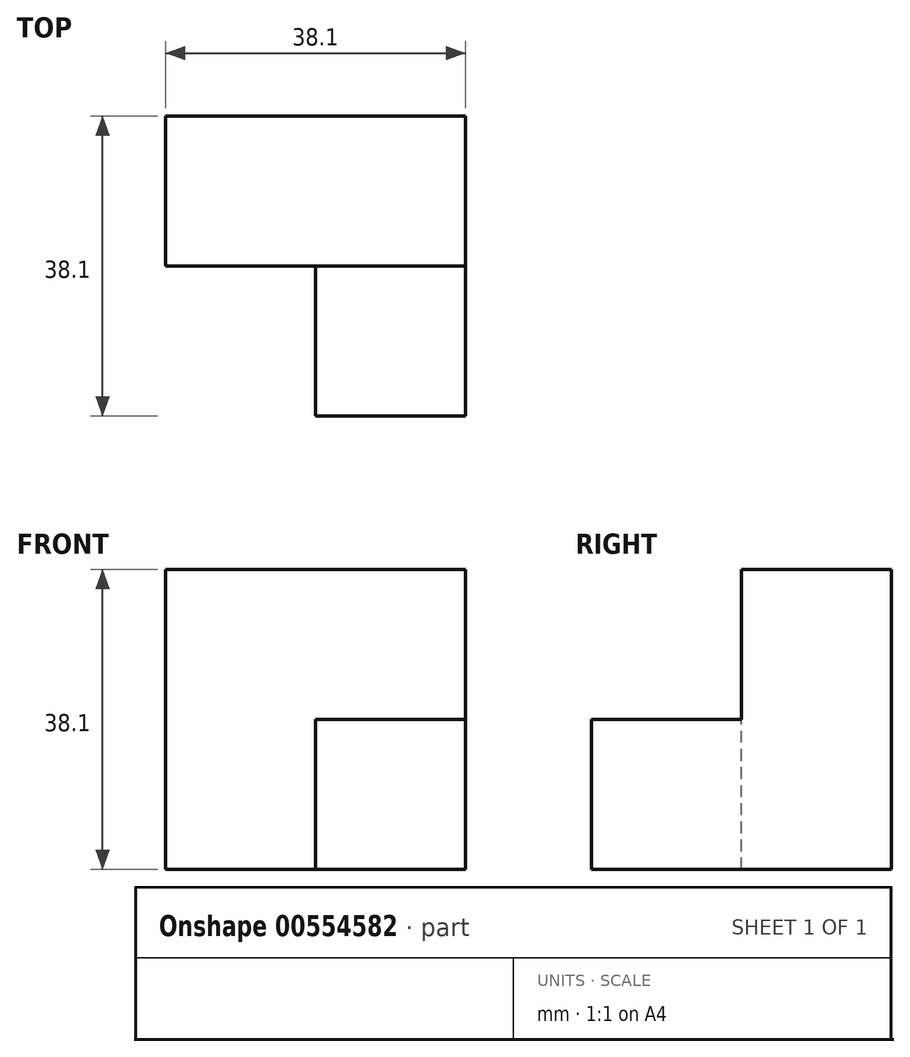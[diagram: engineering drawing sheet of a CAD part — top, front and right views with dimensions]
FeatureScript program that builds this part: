
annotation { "Feature Type Name" : "Feature", "Feature Type Description" : "" }
export const myFeature = defineFeature(function(context is Context, id is Id, definition is map)
    precondition{}
    {
        {
            var Q0;
            Q0=qCreatedBy(makeId("Front.planeOp"),FACE);
            var sketch = newSketch(context, id + "F0", { "sketchPlane" : qUnion([Q0])});
            skLineSegment(sketch, "E0", {"start": v(-17.43, 17.6) * mm, "end": v(20.67, 17.6) * mm});
            skLineSegment(sketch, "E1", {"start": v(20.67, 17.6) * mm, "end": v(20.67, -20.5) * mm});
            skLineSegment(sketch, "E2", {"start": v(20.67, -20.5) * mm, "end": v(-17.43, -20.5) * mm});
            skLineSegment(sketch, "E3", {"start": v(-17.43, -20.5) * mm, "end": v(-17.43, 17.6) * mm});
            skLineSegment(sketch, "E4", {"start": v(1.62, -20.5) * mm, "end": v(1.62, -1.46) * mm});
            skLineSegment(sketch, "E5", {"start": v(1.62, -1.46) * mm, "end": v(20.67, -1.46) * mm});
            skSolve(sketch);
        }
        {
            var Q0;
            {var subQ4=sQuery(id+"F0.wireOp",EDGE,"E0");Q0=makeQuery(id+"F0.imprint","IMPRINT",FACE,{"disambiguationData":[TD([[makeQuery(id+"F0.imprint","IMPRINT",EDGE,{"derivedFrom":subQ4}),-1.0]])]});}
            extrude(context, id + "F1", {"entities" : qUnion([Q0]), "depth" : 19.05 * mm, "offsetDistance" : 25.4 * mm});
        }
        {
            var Q0;
            {var subQ4=sQuery(id+"F0.wireOp",EDGE,"E4");Q0=makeQuery(id+"F0.imprint","IMPRINT",FACE,{"disambiguationData":[TD([[makeQuery(id+"F0.imprint","IMPRINT",EDGE,{"derivedFrom":subQ4}),-1.0]])]});}
            extrude(context, id + "F2", {"entities" : qUnion([Q0]), "operationType" : NewBodyOperationType.ADD, "depth" : 38.1 * mm, "offsetDistance" : 25.4 * mm});
        }
    });
